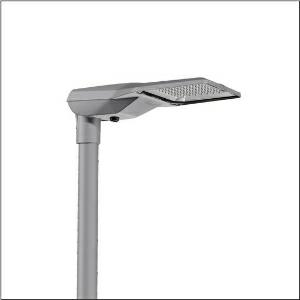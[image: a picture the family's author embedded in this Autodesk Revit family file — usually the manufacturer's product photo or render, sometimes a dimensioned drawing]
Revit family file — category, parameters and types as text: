
# Revit family: streetlight_sl_21_iq_midi___p0_8ab_5xe3r31u08nb_f32c
name_source: partatom
category: Lighting Fixtures
units: mm (PartAtom-declared; Revit-internal decimal feet)

## family parameters
Cut with Voids When Loaded = No
Host = Face
Light Source = No
Part Type = Normal
Room Calculation Point = No
Round Connector Dimension = Use Diameter
Shared = No

## types (1)
- --- (1 x LED, 18710 lm, 136.6 W, 3000K)
    Apparent Load = 137 VA
    CIE Flux Codes = 39 72 97 100 100
    Color Rendering = 70
    Color Temperature = 3000K
    Default Elevation = 1800 mm
    Description = Streetlight SL 21 iQ midi, mast luminaire, primary light control with lens, of PMMA, primary optical cover: cover, of toughened safety glass, transparent, light distribution: P0.8aB, light emission: direct distribution, primary light characteristic: asymmetric, installation type: post-top, side-entry, LED, High Power LED, rated luminous flux: 18.710lm, luminous efficacy: 137lm/W, light colour: 730, colour temperature: 3000K, control gear: iQ-Street Remote, D4i with power reduction, control: pre-setting: logarithmic dimming characteristic, Street-Remote, Auto-Match, Temp-Guard, Lumen-Switch, Night-Set, Smart-Wire, Light-Fading, Desk-Remote (wireless, voltage-free reading and setting of iQ features in the workshop via application-optimized NFC function/RFID function), optimised constant luminous flux control (CLO 2.0), mains connection: 230..240V, AC, 50/60Hz, start of lifetime: 137W, end of service life: 144W, reduction: 61W, luminaire housing, of diecast aluminium, powder-coated, Siteco® metallic grey (DB 702S), corrosivity category C5 mid according to DIN EN ISO 12944, please order mast flange separately, inclination adjustable: 0°, 5°, 10°, 15°, sealing non-destructively replaceable, multi-level sealing system, length: 644mm, width: 335mm, height: 110mm, mast flange for spigot size: 42mm (side-entry): 5XC10008XM4, 60/48mm (side-entry/post-top): 5XC10108XM2, 76/60mm (side-entry/post-top): 5XC10108XM1, mounting height: 4..8m, Smart Interface below, protection rating (complete): IP66, insulation class (complete): insulation class II (safety insulation), certification: CE, ENEC, ENEC+, VDE, impact resistance: IK10, permissible operating ambient temperature for outdoor applications: -40..+50°C, standard-compliant lighting for roads and squares, packaging unit: 1 piece

Light Distribution: P0.8aB
    Height = 111 mm
    Lamp = 1 x LED
    Lamp Light Flux = 18710 lm
    Lamp Power = 136.6 W
    Lamp count = 1
    Length = 644 mm
    Luminous efficacy = 137 lm/W
    Manufacturer = Siteco
    ModVariant = No
    Model = 5XE3R31U08NB
    Number of Poles = 1
    OnlyDefault = Yes
    Power Factor = 1
    Product Name = Streetlight SL 21 iQ midi | P0.8aB
    Product group = mast luminaire | pylon top
    ProductGroupID = 6100
    Protection Class = Protection class II
    Protection Degree = IP 66
    RLX_Detail_Level = 1
    RLX_Emergency_Light_Flux = 0 lm
    RLX_Emergency_Type = 0
    RLX_Emergency_Type_DB = No
    RlxData = <blob elided: 90741 chars, md5=d4dec88b>
    Socket = socket
    Standby Power = 0 W
    System Light Flux = 18710 lm
    System Power = 137 W
    Type Comments = factory setting: luminous flux: 100 % | dim-lin: 254 | 733 mA
    Type Image = l_1004300.jpg
    URL = http://relux.com
    VarID = @adj_092773
    Voltage = 0 V
    Weight = 0.00 kg
    Width = 336 mm

## geometry (parser evidence)
native form markers: Blend x4, Sweep x11
no freeform markers — native parametric forms only
